# Revit family: Partition-Floor_Braced-Bradley_Corp-St_Stl-ADA-N_Stalls
name_source: partatom
category: Specialty Equipment
revit_build: Autodesk Revit MEP 2012 (Build: 20110309_2315(x64)
units: mm (PartAtom-declared; Revit-internal decimal feet)

## types (1)
- ADA (optional) + n Standard Stalls
    Assembly Code = C1010400
    Bottom AFF = 12 "
    Bottom Hinge = 12 "
    Brackets Bottom Height = 18 "
    Brackets Top Height = 64 "
    Bumper Height = 16 "
    Buy American Act = To Be Determined
    CALC_Half Door Width = 11 "
    CALC_Half Panel = 0.5 "
    CALC_Half Pilaster = 0.625 "
    Description = Restroom Partitions, Floor-Braced
    Door Gap = 0.188 "
    Door Handle Height = 37 "
    Door Height = 58 "
    Door Thickness = 1 "
    End Right Pilaster = 0.5 "
    Gap Pilaster Panel = 0.5 "
    Hardware Material = Metal - Bradley Corp - Chrome
    Height = 70 "
    Instructions On-Off Visibility = Yes
    Latch Height = 37 "
    Latch to Edge = 2 "
    Manufacturer = Bradley Corporation
    MasterFormat Number = 10 21 13
    MasterFormat Title = Toilet Compartments
    Material = Stainless Steel
    Material Note = Other Hardware Also Available - Please See www.bradleycorp.com
    Model = Stainless Steel - Series 500 - Floor Braced
    OmniClass Table 21 Number = 21-03 10 90 40
    OmniClass Table 21 Title = Toilet, Bath, and Laundry Accessories
    OmniClass Table 23 Number = 23.15.11.15.11
    OmniClass Table 23 Title = Toilet Compartment and Urinal Screens
    Panel Thickness = 1 "
    Partition Material = Metal - Bradley Corp - Stainless Steel Brushed
    Percentage of Recycled Content = 0
    Pilaster Height = 70 "
    Pilaster Thickness = 1.25 "
    Product Tech Data URL - English = http://bradleycorp.com
    Shoe Height = 3 "
    Shoe Material = Metal - Bradley Corp - Stainless Steel Satin
    Specifications URL = http://www.bradleycorp.com
    Top Hinge = 67 "
    URL = http://www.bradleycorp.com
    Version = 2.0
    Warranty Information = Warranted 15 years against rust out, 5 years on chrome hardware, lifetime of the partition on the stainless steel hardware.

## geometry (parser evidence)
native form markers: Blend x8, Sweep x7
no freeform markers — native parametric forms only
